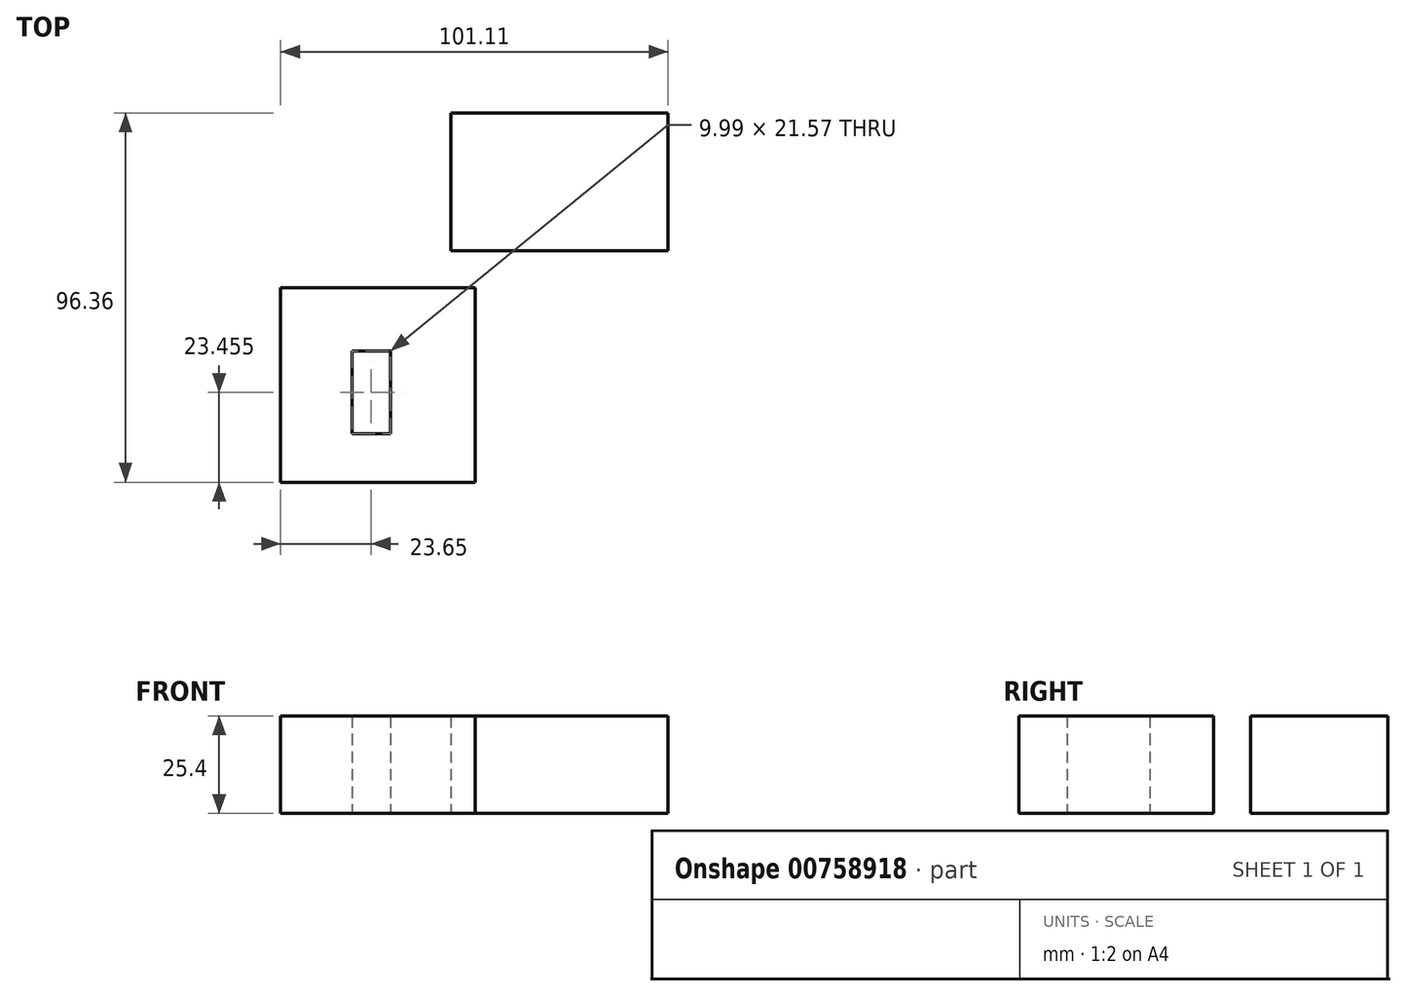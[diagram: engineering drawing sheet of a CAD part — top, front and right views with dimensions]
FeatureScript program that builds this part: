
annotation { "Feature Type Name" : "Feature", "Feature Type Description" : "" }
export const myFeature = defineFeature(function(context is Context, id is Id, definition is map)
    precondition{}
    {
        {
            var Q0;
            Q0=qCreatedBy(makeId("Top.planeOp"),FACE);
            var sketch = newSketch(context, id + "F0", { "sketchPlane" : qUnion([Q0])});
            skLineSegment(sketch, "E0.bottom", {"start": v(-34.31, 25.26) * mm, "end": v(22.34, 25.26) * mm});
            skLineSegment(sketch, "E0.top", {"start": v(-34.31, -10.66) * mm, "end": v(22.34, -10.66) * mm});
            skLineSegment(sketch, "E0.left", {"start": v(-34.31, 25.26) * mm, "end": v(-34.31, -10.66) * mm});
            skLineSegment(sketch, "E0.right", {"start": v(22.34, 25.26) * mm, "end": v(22.34, -10.66) * mm});
            skSolve(sketch);
        }
        {
            var Q0;
            Q0=makeQuery(id+"F0.imprint","IMPRINT",FACE,{"disambiguationData":[TD([[makeQuery(id+"F0.imprint","IMPRINT",EDGE,{"derivedFrom":sQuery(id+"F0.wireOp",EDGE,"E0.bottom")}),-1.0]])]});
            extrude(context, id + "F1", {"entities" : qUnion([Q0]), "depth" : 25.4 * mm, "offsetDistance" : 25.4 * mm});
        }
        {
            var Q0;
            Q0=qCreatedBy(makeId("Top.planeOp"),FACE);
            var sketch = newSketch(context, id + "F2", { "sketchPlane" : qUnion([Q0])});
            skLineSegment(sketch, "E1.bottom", {"start": v(-78.77, -20.3) * mm, "end": v(-27.97, -20.3) * mm});
            skLineSegment(sketch, "E1.top", {"start": v(-78.77, -71.1) * mm, "end": v(-27.97, -71.1) * mm});
            skLineSegment(sketch, "E1.left", {"start": v(-78.77, -20.3) * mm, "end": v(-78.77, -71.1) * mm});
            skLineSegment(sketch, "E1.right", {"start": v(-27.97, -20.3) * mm, "end": v(-27.97, -71.1) * mm});
            skLineSegment(sketch, "E2.bottom", {"start": v(-60.11, -36.86) * mm, "end": v(-50.13, -36.86) * mm});
            skLineSegment(sketch, "E2.top", {"start": v(-60.11, -58.43) * mm, "end": v(-50.13, -58.43) * mm});
            skLineSegment(sketch, "E2.left", {"start": v(-60.11, -36.86) * mm, "end": v(-60.11, -58.43) * mm});
            skLineSegment(sketch, "E2.right", {"start": v(-50.13, -36.86) * mm, "end": v(-50.13, -58.43) * mm});
            skSolve(sketch);
        }
        {
            var Q0;
            Q0=makeQuery(id+"F2.imprint","IMPRINT",FACE,{"disambiguationData":[TD([[makeQuery(id+"F2.imprint","IMPRINT",EDGE,{"derivedFrom":sQuery(id+"F2.wireOp",EDGE,"E1.bottom")}),-1.0]])]});
            extrude(context, id + "F3", {"entities" : qUnion([Q0]), "depth" : 25.4 * mm, "offsetDistance" : 25.4 * mm});
        }
    });
